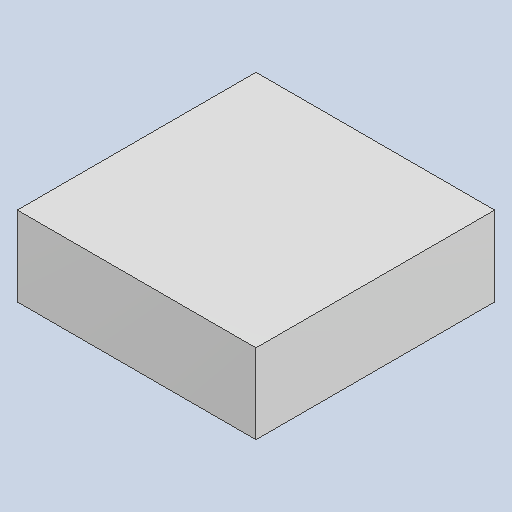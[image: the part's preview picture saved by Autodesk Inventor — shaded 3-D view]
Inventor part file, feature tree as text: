
AUTODESK INVENTOR PART (.ipt)
format: ipt  version: 2023.4 (Build 274418000, 418)  size: 79,872 bytes
history: native  units: mm
features: extrude x1
ambient origin geometry x8: Origin, YZ Plane, XZ Plane, XY Plane, X Axis, Y Axis, Z Axis, Center Point
bodies: Solid1 (feature_tree)
feature tree (1):
  extrude  "Extruded_9"  [1 undecoded]
note: 1 required parameter value undecoded (feature->parameter linkage not recoverable at this tier; creation-order binding heuristic only, values carry confidence <= 0.55)
